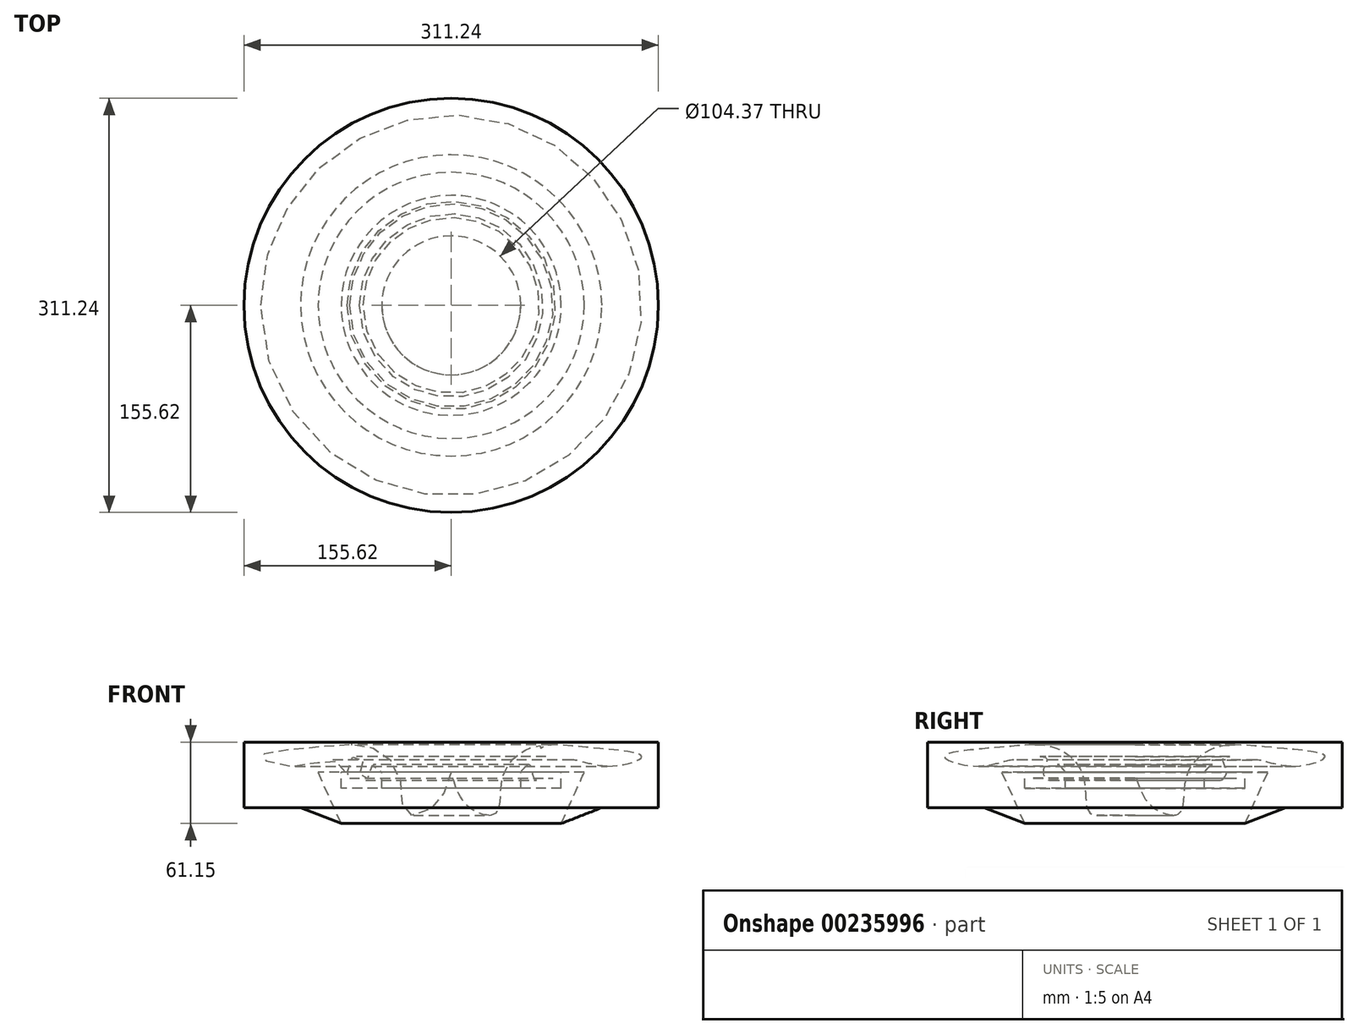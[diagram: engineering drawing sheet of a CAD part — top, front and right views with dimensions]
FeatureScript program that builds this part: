
annotation { "Feature Type Name" : "Feature", "Feature Type Description" : "" }
export const myFeature = defineFeature(function(context is Context, id is Id, definition is map)
    precondition{}
    {
        {
            var Q0;
            Q0=qCreatedBy(makeId("Front.planeOp"),FACE);
            var sketch = newSketch(context, id + "F0", { "sketchPlane" : qUnion([Q0])});
            skLineSegment(sketch, "E0", {"start": v(0, 0) * mm, "end": v(-155.62, 0) * mm});
            skLineSegment(sketch, "E1", {"start": v(-155.62, 0) * mm, "end": v(-155.62, -49.2) * mm});
            skLineSegment(sketch, "E2", {"start": v(-155.62, -49.2) * mm, "end": v(-113.18, -49.2) * mm});
            skLineSegment(sketch, "E3", {"start": v(0, 0) * mm, "end": v(0, -22.48) * mm});
            skLineSegment(sketch, "E4", {"start": v(-52.19, -22.48) * mm, "end": v(-52.19, -34.74) * mm});
            skLineSegment(sketch, "E5", {"start": v(-52.19, -34.74) * mm, "end": v(-82.68, -34.74) * mm});
            skLineSegment(sketch, "E6", {"start": v(-82.68, -34.74) * mm, "end": v(-82.68, -22.48) * mm});
            skLineSegment(sketch, "E7", {"start": v(-82.68, -22.48) * mm, "end": v(-99.97, -22.48) * mm});
            skLineSegment(sketch, "E8", {"start": v(-99.97, -22.48) * mm, "end": v(-82.68, -61.15) * mm});
            skLineSegment(sketch, "E9", {"start": v(-82.68, -61.15) * mm, "end": v(-113.18, -49.2) * mm});
            skFitSpline(sketch, "E10", {"points": [v(0, -22.48) * mm, v(-13.22, -48.76) * mm, v(-33.62, -53.3) * mm, v(-38.48, -27.07) * mm, v(-58.56, -4.72) * mm, v(-99.68, -3.75) * mm, v(-143.07, -10.88) * mm, v(-113.6, -18) * mm, v(-85.43, -15.09) * mm, v(-76.37, -27.07) * mm, v(-77.34, -13.47) * mm, v(-66.33, -12.5) * mm, v(-68.92, -22.48) * mm, v(-63.42, -28.36) * mm, v(-59.2, -17.35) * mm, v(-52.19, -22.48) * mm], "startDerivative": vector(-105.59, -374) * mm, "endDerivative": vector(189.75, -226.1) * mm});
            skSolve(sketch);
        }
        {
            var Q0;
            Q0 = qSketchRegion(id + "F0", true);
            var Q1;
            Q1=sQuery(id+"F0.wireOp",EDGE,"E3");
            revolve(context, id + "F1", {"entities" : qUnion([Q0]), "axis" : qUnion([Q1]), "revolveType" : RevolveType.FULL});
        }
    });
